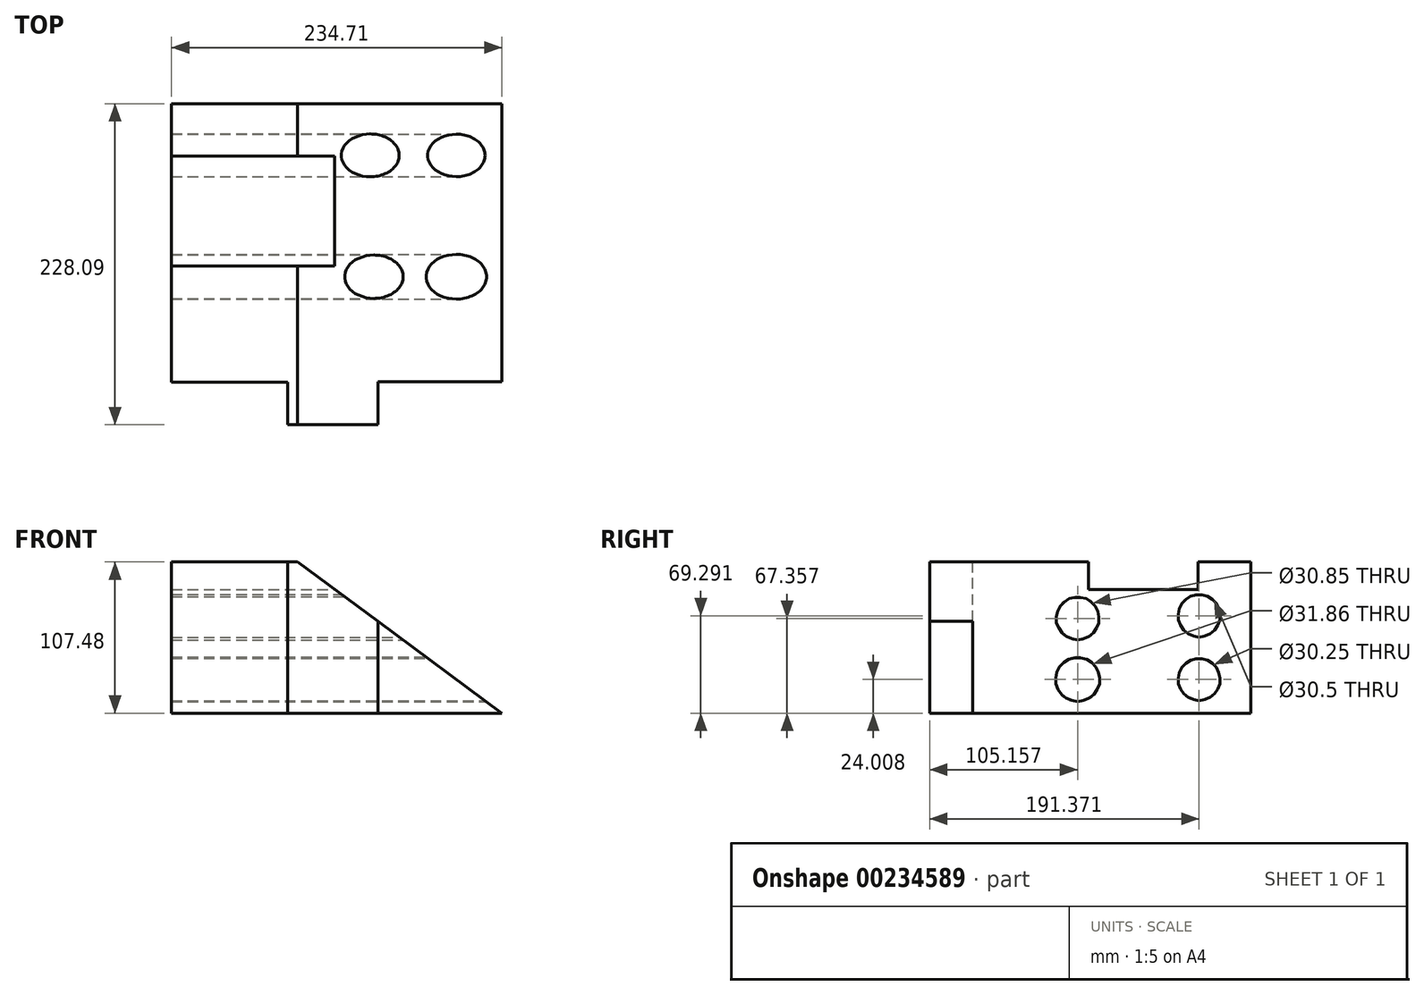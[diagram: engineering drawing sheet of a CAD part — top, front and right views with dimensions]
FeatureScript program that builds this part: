
annotation { "Feature Type Name" : "Feature", "Feature Type Description" : "" }
export const myFeature = defineFeature(function(context is Context, id is Id, definition is map)
    precondition{}
    {
        {
            var Q0;
            Q0=qCreatedBy(makeId("Front.planeOp"),FACE);
            var sketch = newSketch(context, id + "F0", { "sketchPlane" : qUnion([Q0])});
            skLineSegment(sketch, "E0.bottom", {"start": v(118.93, 53.74) * mm, "end": v(-116.35, 53.74) * mm});
            skLineSegment(sketch, "E0.top", {"start": v(118.93, -53.74) * mm, "end": v(-116.35, -53.74) * mm});
            skLineSegment(sketch, "E0.left", {"start": v(118.93, 53.74) * mm, "end": v(118.93, -53.74) * mm});
            skLineSegment(sketch, "E0.right", {"start": v(-116.35, 53.74) * mm, "end": v(-116.35, -53.74) * mm});
            skPoint(sketch, "E0.middle", {"position": v(1.29, 0) * mm});
            skSolve(sketch);
        }
        {
            var Q0;
            Q0 = qSketchRegion(id + "F0", true);
            extrude(context, id + "F1", {"entities" : qUnion([Q0]), "depth" : 151.9 * mm, "hasSecondDirection" : true, "secondDirectionOppositeDirection" : true, "secondDirectionDepth" : 76.2 * mm});
        }
        {
            var Q0;
            Q0=qCreatedBy(makeId("Front.planeOp"),FACE);
            var sketch = newSketch(context, id + "F2", { "sketchPlane" : qUnion([Q0])});
            skLineSegment(sketch, "E1", {"start": v(-31.62, 57.24) * mm, "end": v(126.14, -59.5) * mm});
            skLineSegment(sketch, "E2", {"start": v(126.14, -59.5) * mm, "end": v(126.14, 57.24) * mm});
            skLineSegment(sketch, "E3", {"start": v(-31.62, 57.24) * mm, "end": v(126.14, 57.24) * mm});
            skSolve(sketch);
        }
        {
            var Q0;
            Q0 = qSketchRegion(id + "F2", true);
            extrude(context, id + "F3", {"entities" : qUnion([Q0]), "operationType" : NewBodyOperationType.REMOVE, "depth" : 237.24 * mm, "hasSecondDirection" : true, "secondDirectionOppositeDirection" : true, "secondDirectionDepth" : 76.2 * mm});
        }
        {
            var Q0;
            Q0=qCreatedBy(makeId("Right.planeOp"),FACE);
            var sketch = newSketch(context, id + "F4", { "sketchPlane" : qUnion([Q0])});
            skLineSegment(sketch, "E4.bottom", {"start": v(-39.16, 70.82) * mm, "end": v(38.84, 70.82) * mm});
            skLineSegment(sketch, "E4.top", {"start": v(-39.16, 34.24) * mm, "end": v(38.84, 34.24) * mm});
            skLineSegment(sketch, "E4.left", {"start": v(-39.16, 70.82) * mm, "end": v(-39.16, 34.24) * mm});
            skLineSegment(sketch, "E4.right", {"start": v(38.84, 70.82) * mm, "end": v(38.84, 34.24) * mm});
            skSolve(sketch);
        }
        {
            var Q0;
            Q0 = qSketchRegion(id + "F4", true);
            extrude(context, id + "F5", {"entities" : qUnion([Q0]), "operationType" : NewBodyOperationType.REMOVE, "oppositeDirection" : true, "depth" : 158.24 * mm});
        }
        {
            var Q0;
            Q0=qCreatedBy(makeId("Right.planeOp"),FACE);
            var sketch = newSketch(context, id + "F6", { "sketchPlane" : qUnion([Q0])});
            skCircle(sketch, "E5", {"center": v(-46.73, 13.62) * mm, "radius": 15.42 * mm});
            skCircle(sketch, "E6", {"center": v(-46.73, -29.73) * mm, "radius": 15.93 * mm});
            skCircle(sketch, "E7", {"center": v(39.48, -29.73) * mm, "radius": 15.13 * mm});
            skCircle(sketch, "E8", {"center": v(39.48, 15.55) * mm, "radius": 15.25 * mm});
            skSolve(sketch);
        }
        {
            var Q0;
            Q0 = qSketchRegion(id + "F6", true);
            extrude(context, id + "F7", {"entities" : qUnion([Q0]), "operationType" : NewBodyOperationType.REMOVE, "oppositeDirection" : true, "depth" : 184.66 * mm, "hasSecondDirection" : true, "secondDirectionOppositeDirection" : false, "secondDirectionDepth" : 146.8 * mm});
        }
        {
            var Q0;
            Q0=makeQuery(id+"F1.opExtrude","SWEPT_FACE",FACE,{"disambiguationData":[OSD([sQuery(id+"F0.wireOp",EDGE,"E0.top")])]});
            var sketch = newSketch(context, id + "F8", { "sketchPlane" : qUnion([Q0])});
            skLineSegment(sketch, "E9.bottom", {"start": v(118.36, 151.9) * mm, "end": v(30.19, 151.9) * mm});
            skLineSegment(sketch, "E9.top", {"start": v(118.36, 121.42) * mm, "end": v(30.19, 121.42) * mm});
            skLineSegment(sketch, "E9.left", {"start": v(118.36, 151.9) * mm, "end": v(118.36, 121.42) * mm});
            skLineSegment(sketch, "E9.right", {"start": v(30.19, 151.9) * mm, "end": v(30.19, 121.42) * mm});
            skSolve(sketch);
        }
        {
            var Q0;
            Q0 = qSketchRegion(id + "F8", true);
            extrude(context, id + "F9", {"entities" : qUnion([Q0]), "operationType" : NewBodyOperationType.REMOVE, "oppositeDirection" : true, "depth" : 160.53 * mm});
        }
        {
            var Q0;
            Q0=makeQuery(id+"F1.opExtrude","SWEPT_FACE",FACE,{"disambiguationData":[OSD([sQuery(id+"F0.wireOp",EDGE,"E0.top")])]});
            var sketch = newSketch(context, id + "F10", { "sketchPlane" : qUnion([Q0])});
            skLineSegment(sketch, "E10.bottom", {"start": v(-116.35, 151.9) * mm, "end": v(-33.94, 151.9) * mm});
            skLineSegment(sketch, "E10.top", {"start": v(-116.35, 121.67) * mm, "end": v(-33.94, 121.67) * mm});
            skLineSegment(sketch, "E10.left", {"start": v(-116.35, 151.9) * mm, "end": v(-116.35, 121.67) * mm});
            skLineSegment(sketch, "E10.right", {"start": v(-33.94, 151.9) * mm, "end": v(-33.94, 121.67) * mm});
            skSolve(sketch);
        }
        {
            var Q0;
            Q0 = qSketchRegion(id + "F10", true);
            extrude(context, id + "F11", {"entities" : qUnion([Q0]), "operationType" : NewBodyOperationType.REMOVE, "oppositeDirection" : true, "depth" : 127.76 * mm});
        }
    });
